# Revit family: I_Joist-Roseburg-LVL
name_source: partatom
category: Structural Framing
units: mm (PartAtom-declared; Revit-internal decimal feet)

## family parameters
Always export as geometry = No
Always vertical = Yes
Classification Number = 23.25.30.21.17.11
Cut with Voids When Loaded = No
Material for Model Behavior = Wood
Section Shape = Not Defined
Shared = No
Show family pre-cut in plan views = Yes
Structural Framing Length Roundoff = 0' - 0"

## types (19) — shared parameters
Application Chart = https://www.roseburg.com
Assembly Code = B10
Building Codes = See PR-L289 & PR-L289C
Construction Details = https://www.arcat.com
EWP Application Chart = https://www.arcat.com
Green Building-LEED = https://www.arcat.com
Installation Guide = https://www.arcat.com
Keynote = 06 40 00
Manufacturer = Roseburg
Material = LVL OSB
Product Data = https://www.arcat.com
Specification = https://www.arcat.com
Structural Material = Engineered Wood - Roseburg - LVL
Testing Data = See ESR1210
URL = https://www.roseburg.com -joist/

## per-type parameters (varying)
| type | Description | Model | Series | d |
| RFPI 20 14 | LVL Flange I-Joist - RFPI 20 14" | RFPI 20 14" | RFPI 20 | 1' - 2" |
| RFPI 40 14 | LVL Flange I-Joist - RFPI 40 14" | RFPI 40 14" | RFPI 40 | 1' - 2" |
| RFPI 90 9-12 | LVL Flange I-Joist - RFPI 90 9-1/2" | RFPI 90 9-1/2" | RFPI 90 | 0' - 9 1/2" |
| RFPI 70 14 | LVL Flange I-Joist - RFPI 70 14" | RFPI 70 14" | RFPI 70 | 1' - 2" |
| RFPI 400 9-12 | LVL Flange I-Joist - RFPI 400 9-1/2" | RFPI 400 9-1/2" | RFPI 400 | 0' - 9 1/2" |
| RFPI 90 16 | LVL Flange I-Joist - RFPI 90 16" | RFPI 90 16" | RFPI 90 | 1' - 4" |
| RFPI 400 14 | LVL Flange I-Joist - RFPI 400 14" | RFPI 400 14" | RFPI 400 | 1' - 2" |
| RFPI 70 11-78 | LVL Flange I-Joist - RFPI 70 11-7/8" | RFPI 70 11-7/8" | RFPI 70 | 0' - 11 7/8" |
| RFPI 20 9-12 | LVL Flange I-Joist - RFPI 20 9-1/2" | RFPI 20 9-1/2" | RFPI 20 | 0' - 9 1/2" |
| RFPI 400 11-78 | LVL Flange I-Joist - RFPI 400 11-7/8" | RFPI 400 11-7/8" | RFPI 400 | 0' - 11 7/8" |
| RFPI 40 16 | LVL Flange I-Joist - RFPI 40 16" | RFPI 40 16" | RFPI 40 | 1' - 4" |
| RFPI 400 16 | LVL Flange I-Joist - RFPI 400 16" | RFPI 400 16" | RFPI 400 | 1' - 4" |
| RFPI 70 16 | LVL Flange I-Joist - RFPI 70 16" | RFPI 70 16" | RFPI 70 | 1' - 4" |
| RFPI 40 9-12 | LVL Flange I-Joist - RFPI 40 9-1/2" | RFPI 40 9-1/2" | RFPI 40 | 0' - 9 1/2" |
| RFPI 70 9-12 | LVL Flange I-Joist - RFPI 70 9-1/2" | RFPI 70 9-1/2" | RFPI 70 | 0' - 9 1/2" |
| RFPI 20 11-78 | LVL Flange I-Joist - RFPI 20 11-7/8" | RFPI 20 11-7/8" | RFPI 20 | 0' - 11 7/8" |
| RFPI 90 14 | LVL Flange I-Joist - RFPI 90 14" | RFPI 90 14" | RFPI 90 | 1' - 2" |
| RFPI 40 11-78 | LVL Flange I-Joist - RFPI 40 11-7/8" | RFPI 40 11-7/8" | RFPI 40 | 0' - 11 7/8" |
| RFPI 90 11-78 | LVL Flange I-Joist - RFPI 90 11-7/8" | RFPI 90 11-7/8" | RFPI 90 | 0' - 11 7/8" |

## geometry (parser evidence)
native form markers: Sweep x1
no freeform markers — native parametric forms only
